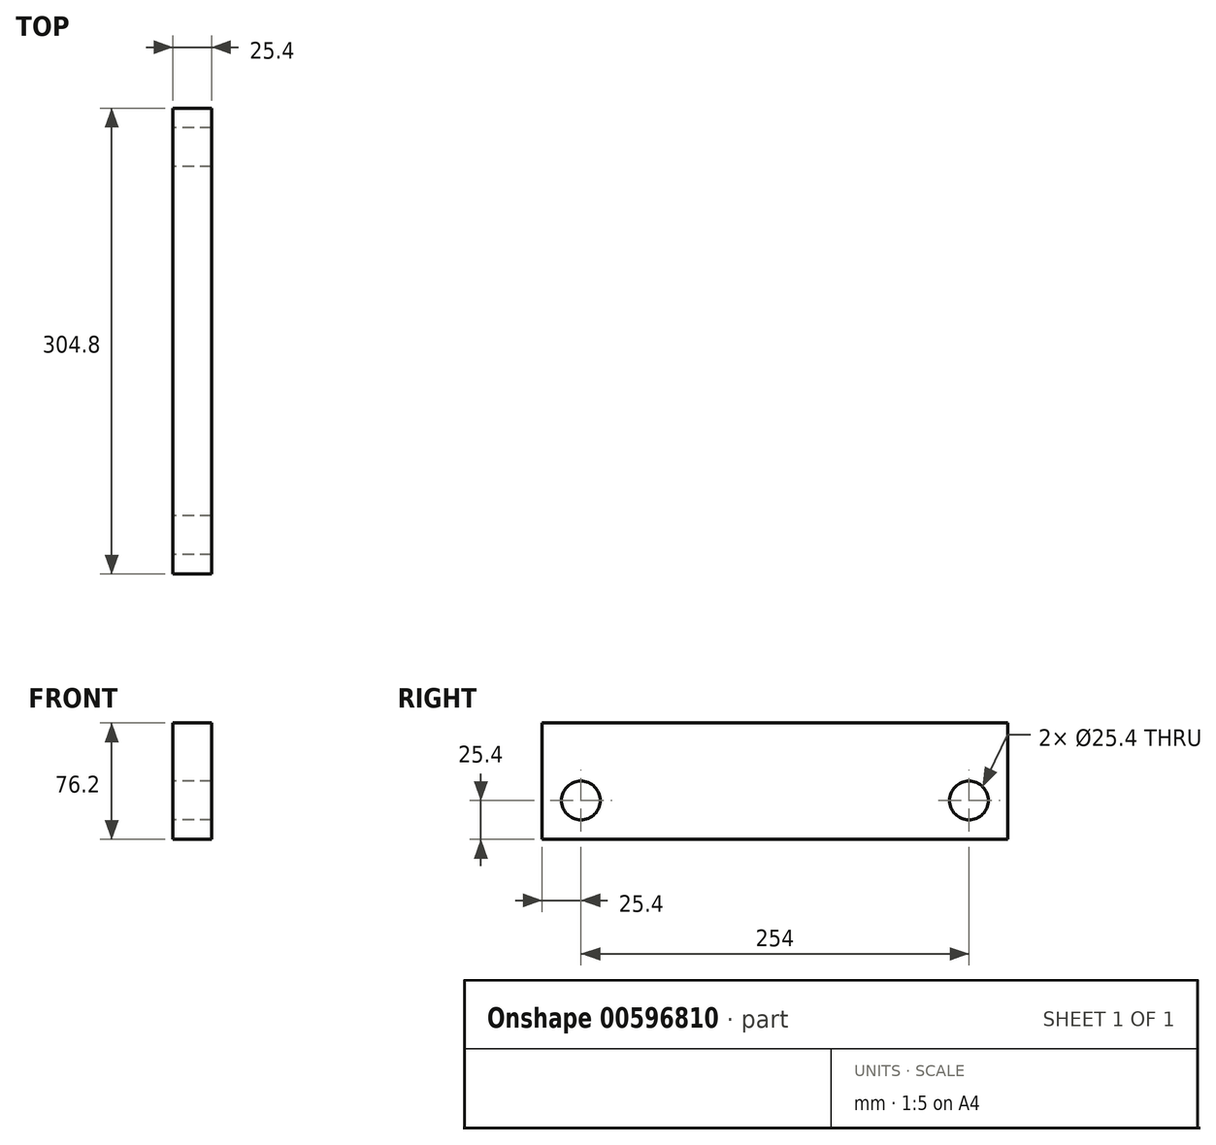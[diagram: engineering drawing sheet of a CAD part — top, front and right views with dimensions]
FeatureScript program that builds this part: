
annotation { "Feature Type Name" : "Feature", "Feature Type Description" : "" }
export const myFeature = defineFeature(function(context is Context, id is Id, definition is map)
    precondition{}
    {
        {
            var Q0;
            Q0=qCreatedBy(makeId("Right.planeOp"),FACE);
            var sketch = newSketch(context, id + "F0", { "sketchPlane" : qUnion([Q0])});
            skLineSegment(sketch, "E0.bottom", {"start": v(0, 0) * mm, "end": v(304.8, 0) * mm});
            skLineSegment(sketch, "E0.top", {"start": v(0, -76.2) * mm, "end": v(304.8, -76.2) * mm});
            skLineSegment(sketch, "E0.left", {"start": v(0, 0) * mm, "end": v(0, -76.2) * mm});
            skLineSegment(sketch, "E0.right", {"start": v(304.8, 0) * mm, "end": v(304.8, -76.2) * mm});
            skCircle(sketch, "E1", {"center": v(25.4, -50.8) * mm, "radius": 12.7 * mm});
            skCircle(sketch, "E2", {"center": v(279.4, -50.8) * mm, "radius": 12.7 * mm});
            skSolve(sketch);
        }
        {
            var Q0;
            Q0=qSketchRegion(id+"F0",true);
            extrude(context, id + "F1", {"entities" : qUnion([Q0]), "depth" : 25.4 * mm, "offsetDistance" : 25.4 * mm});
        }
    });
